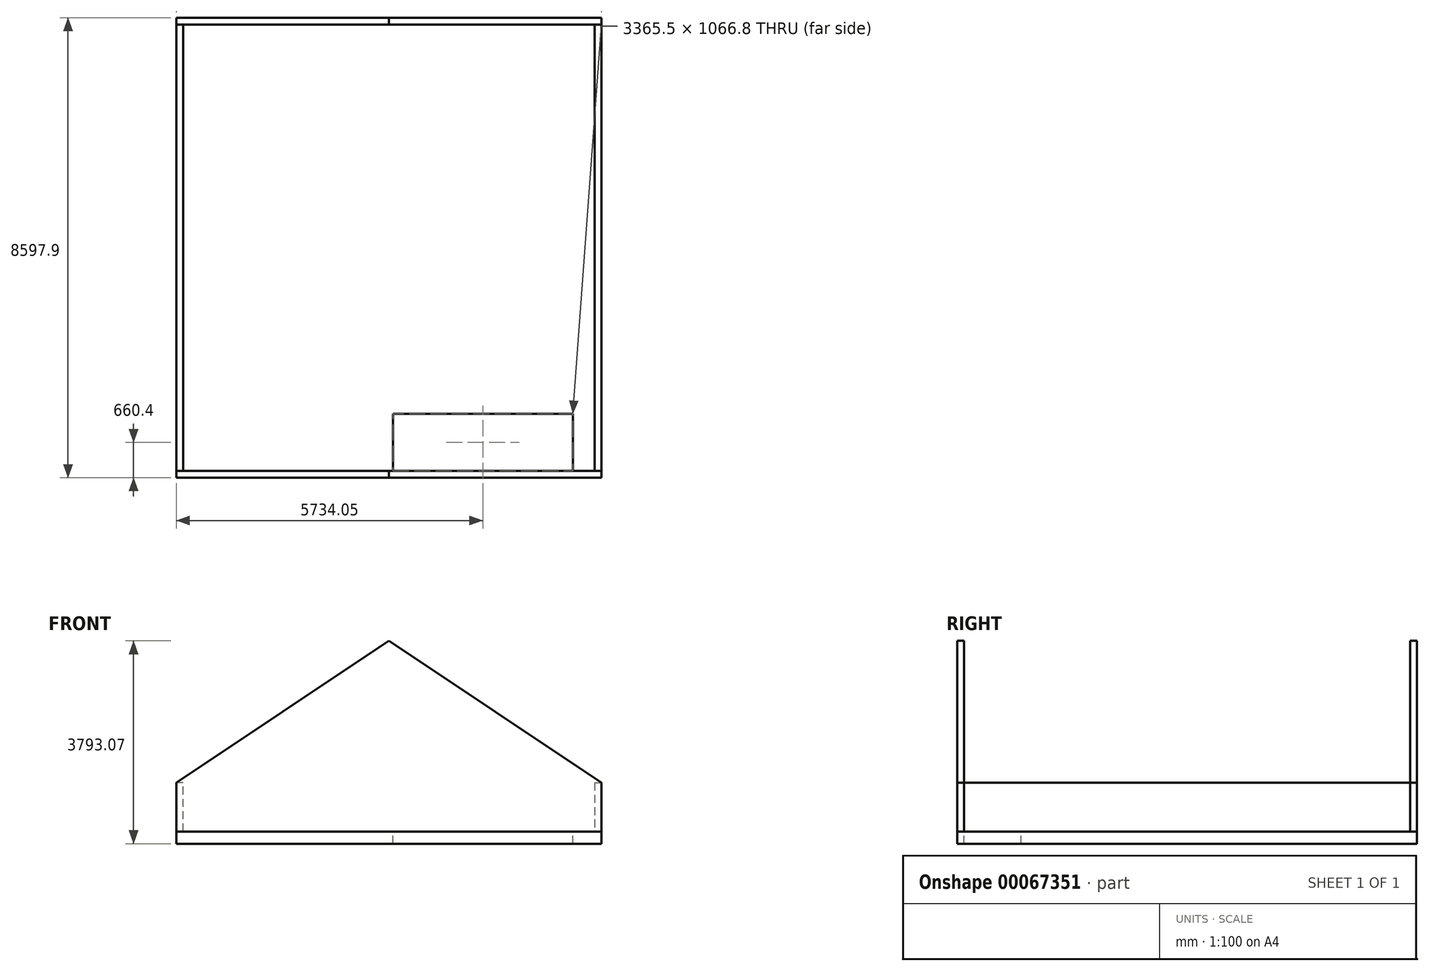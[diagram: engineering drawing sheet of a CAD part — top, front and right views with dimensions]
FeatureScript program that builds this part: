
annotation { "Feature Type Name" : "Feature", "Feature Type Description" : "" }
export const myFeature = defineFeature(function(context is Context, id is Id, definition is map)
    precondition{}
    {
        {
            var Q0;
            Q0=qCreatedBy(makeId("Top.planeOp"),FACE);
            var sketch = newSketch(context, id + "F0", { "sketchPlane" : qUnion([Q0])});
            skLineSegment(sketch, "E0.rect.bottom", {"start": v(3975.1, 4298.95) * mm, "end": v(-3975.1, 4298.95) * mm});
            skLineSegment(sketch, "E0.rect.top", {"start": v(3975.1, -4298.95) * mm, "end": v(-3975.1, -4298.95) * mm});
            skLineSegment(sketch, "E0.rect.left", {"start": v(3975.1, 4298.95) * mm, "end": v(3975.1, -4298.95) * mm});
            skLineSegment(sketch, "E0.rect.right", {"start": v(-3975.1, 4298.95) * mm, "end": v(-3975.1, -4298.95) * mm});
            skPoint(sketch, "E0.rect.middle", {"position": v(0, 0) * mm});
            skSolve(sketch);
        }
        {
            var Q0;
            Q0=makeQuery(id+"F0.imprint","IMPRINT",FACE,{"disambiguationData":[TD([[makeQuery(id+"F0.imprint","IMPRINT",EDGE,{"derivedFrom":sQuery(id+"F0.wireOp",EDGE,"E0.rect.bottom")}),1.0]])]});
            extrude(context, id + "F1", {"entities" : qUnion([Q0]), "depth" : 228.6 * mm});
        }
        {
            var Q0;
            Q0=makeQuery(id+"F1.opExtrude","CAP_FACE",FACE,{"disambiguationData":[OSD([sQuery(id+"F0.wireOp",EDGE,"E0.rect.bottom"),sQuery(id+"F0.wireOp",EDGE,"E0.rect.top"),sQuery(id+"F0.wireOp",EDGE,"E0.rect.left"),sQuery(id+"F0.wireOp",EDGE,"E0.rect.right")])],"isStart":false});
            var sketch = newSketch(context, id + "F2", { "sketchPlane" : qUnion([Q0])});
            skLineSegment(sketch, "E1.bottom", {"start": v(76.2, -3105.15) * mm, "end": v(3441.7, -3105.15) * mm});
            skLineSegment(sketch, "E1.top", {"start": v(76.2, -4171.95) * mm, "end": v(3441.7, -4171.95) * mm});
            skLineSegment(sketch, "E1.left", {"start": v(76.2, -3105.15) * mm, "end": v(76.2, -4171.95) * mm});
            skLineSegment(sketch, "E1.right", {"start": v(3441.7, -3105.15) * mm, "end": v(3441.7, -4171.95) * mm});
            skSolve(sketch);
        }
        {
            var Q0;
            Q0 = qSketchRegion(id + "F2", true);
            extrude(context, id + "F3", {"entities" : qUnion([Q0]), "operationType" : NewBodyOperationType.REMOVE, "endBound" : BoundingType.UP_TO_NEXT, "oppositeDirection" : true, "depth" : 25.4 * mm});
        }
        {
            var Q0;
            Q0=makeQuery(id+"F1.opExtrude","SWEPT_FACE",FACE,{"disambiguationData":[OSD([sQuery(id+"F0.wireOp",EDGE,"E0.rect.top")])]});
            var sketch = newSketch(context, id + "F4", { "sketchPlane" : qUnion([Q0])});
            skLineSegment(sketch, "E2", {"start": v(-3975.1, 228.6) * mm, "end": v(-3975.1, 1143) * mm});
            skLineSegment(sketch, "E3", {"start": v(-3975.1, 1143) * mm, "end": v(0, 3793.07) * mm});
            skLineSegment(sketch, "E4", {"start": v(0, 3793.07) * mm, "end": v(3975.1, 1143) * mm});
            skLineSegment(sketch, "E5", {"start": v(3975.1, 1143) * mm, "end": v(3975.1, 228.6) * mm});
            skLineSegment(sketch, "E6", {"start": v(3975.1, 228.6) * mm, "end": v(-3975.1, 228.6) * mm});
            skLineSegment(sketch, "E7", {"start": v(-3975.1, 1143) * mm, "end": v(-3975.1, 1346.2) * mm, "construction": true});
            skLineSegment(sketch, "E8", {"start": v(-3975.1, 1346.2) * mm, "end": v(-3670.3, 1346.2) * mm, "construction": true});
            skLineSegment(sketch, "E9", {"start": v(-2146.3, 2362.2) * mm, "end": v(2146.3, 2362.2) * mm, "construction": true});
            skSolve(sketch);
        }
        {
            var Q0;
            Q0 = qSketchRegion(id + "F4", true);
            extrude(context, id + "F5", {"entities" : qUnion([Q0]), "oppositeDirection" : true, "depth" : 127 * mm});
        }
        {
            var Q0;
            Q0=makeQuery(id+"F1.opExtrude","SWEPT_FACE",FACE,{"disambiguationData":[OSD([sQuery(id+"F0.wireOp",EDGE,"E0.rect.bottom")])]});
            var sketch = newSketch(context, id + "F6", { "sketchPlane" : qUnion([Q0])});
            skLineSegment(sketch, "E10", {"start": v(-3975.1, 228.6) * mm, "end": v(-3975.1, 1143) * mm});
            skLineSegment(sketch, "E11", {"start": v(-3975.1, 1143) * mm, "end": v(0, 3793.07) * mm});
            skLineSegment(sketch, "E12", {"start": v(0, 3793.07) * mm, "end": v(3975.1, 1143) * mm});
            skLineSegment(sketch, "E13", {"start": v(3975.1, 1143) * mm, "end": v(3975.1, 228.6) * mm});
            skLineSegment(sketch, "E14", {"start": v(3975.1, 228.6) * mm, "end": v(-3975.1, 228.6) * mm});
            skLineSegment(sketch, "E15", {"start": v(-2146.3, 2362.2) * mm, "end": v(2146.3, 2362.2) * mm});
            skSolve(sketch);
        }
        {
            var Q0;
            Q0 = qSketchRegion(id + "F6", true);
            extrude(context, id + "F7", {"entities" : qUnion([Q0]), "oppositeDirection" : true, "depth" : 127 * mm});
        }
        {
            var Q0;
            Q0=makeQuery(id+"F1.opExtrude","SWEPT_FACE",FACE,{"disambiguationData":[OSD([sQuery(id+"F0.wireOp",EDGE,"E0.rect.right")])]});
            var sketch = newSketch(context, id + "F8", { "sketchPlane" : qUnion([Q0])});
            skLineSegment(sketch, "E16.bottom", {"start": v(-4171.95, 228.6) * mm, "end": v(4171.95, 228.6) * mm});
            skLineSegment(sketch, "E16.top", {"start": v(-4171.95, 1143) * mm, "end": v(4171.95, 1143) * mm});
            skLineSegment(sketch, "E16.left", {"start": v(-4171.95, 228.6) * mm, "end": v(-4171.95, 1143) * mm});
            skLineSegment(sketch, "E16.right", {"start": v(4171.95, 228.6) * mm, "end": v(4171.95, 1143) * mm});
            skSolve(sketch);
        }
        {
            var Q0;
            Q0=makeQuery(id+"F8.imprint","IMPRINT",FACE,{"disambiguationData":[TD([[makeQuery(id+"F8.imprint","IMPRINT",EDGE,{"derivedFrom":sQuery(id+"F8.wireOp",EDGE,"E16.bottom")}),1.0]])]});
            extrude(context, id + "F9", {"entities" : qUnion([Q0]), "oppositeDirection" : true, "depth" : 127 * mm});
        }
        {
            var Q0;
            Q0=makeQuery(id+"F1.opExtrude","SWEPT_FACE",FACE,{"disambiguationData":[OSD([sQuery(id+"F0.wireOp",EDGE,"E0.rect.left")])]});
            var sketch = newSketch(context, id + "F10", { "sketchPlane" : qUnion([Q0])});
            skLineSegment(sketch, "E17.bottom", {"start": v(-4171.95, 1143) * mm, "end": v(4171.95, 1143) * mm});
            skLineSegment(sketch, "E17.top", {"start": v(-4171.95, 228.6) * mm, "end": v(4171.95, 228.6) * mm});
            skLineSegment(sketch, "E17.left", {"start": v(-4171.95, 1143) * mm, "end": v(-4171.95, 228.6) * mm});
            skLineSegment(sketch, "E17.right", {"start": v(4171.95, 1143) * mm, "end": v(4171.95, 228.6) * mm});
            skSolve(sketch);
        }
        {
            var Q0;
            Q0=makeQuery(id+"F10.imprint","IMPRINT",FACE,{"disambiguationData":[TD([[makeQuery(id+"F10.imprint","IMPRINT",EDGE,{"derivedFrom":sQuery(id+"F10.wireOp",EDGE,"E17.bottom")}),-1.0]])]});
            extrude(context, id + "F11", {"entities" : qUnion([Q0]), "oppositeDirection" : true, "depth" : 127 * mm});
        }
    });
